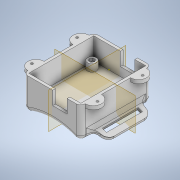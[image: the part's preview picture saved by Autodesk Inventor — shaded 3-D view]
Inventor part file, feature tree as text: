
AUTODESK INVENTOR PART (.ipt)
format: ipt  version: 2021 (Build 250183000, 183)  size: 576,000 bytes
history: native  units: mm
features: extrude x21, sketch x19, fillet x11, mirror x6, plane x2, pattern_linear x1, projected_geometry x1
ambient origin geometry x8: Origin, YZ Plane, XZ Plane, XY Plane, X Axis, Y Axis, Z Axis, Center Point
bodies: Solid1 (feature_tree)
feature tree (61):
  sketch  "Sketch1"  dims[d0=76.0mm d1=90.0mm]
  extrude  "Extrusion2"  Depth=90.0mm
  extrude  "Extrusion3"  Depth=3.0mm TaperAngle=0.0deg
  extrude  "Extrusion4"  Depth=10.0mm
  extrude  "Extrusion5"  Depth=3.0mm TaperAngle=0.0deg
  pattern_linear  "Rectangular Pattern1"  Count1=2 Spacing1=56.07mm
  sketch  "Sketch5"  dims[d12=6.0mm]
  extrude  "Extrusion6"  Depth=9.0mm TaperAngle=0.0deg
  extrude  "Extrusion7"  Depth=3.0mm TaperAngle=0.0deg
  sketch  "Sketch6"  dims[d13=2.7mm d14=0.0mm]
  extrude  "Extrusion8"  Depth=3.0mm TaperAngle=0.0deg
  extrude  "Extrusion9"  Depth=3.0mm TaperAngle=0.0deg
  plane  "Work Plane1"
  mirror  "Mirror1"
  sketch  "Sketch14"  dims[d15=3.3mm]
  extrude  "Extrusion15"  Depth=6.68mm
  extrude  "Extrusion17"  Depth=10.0mm TaperAngle=0.0deg
  extrude  "Extrusion18"  Depth=4.0mm TaperAngle=0.0deg
  mirror  "Mirror5"
  plane  "Work Plane3"
  mirror  "Mirror6"
  extrude  "Extrusion22"  Depth=4.0mm
  fillet  "Fillet9"  Radius=4.0mm
  extrude  "Extrusion26"  Depth=3.0mm
  extrude  "Extrusion27"  Depth=15.0mm TaperAngle=0.0deg
  fillet  "Fillet12"  Radius=40.0mm
  fillet  "Fillet13"  Radius=5.0mm
  mirror  "Mirror9"
  fillet  "Fillet14"  Radius=5.0mm
  fillet  "Fillet15"  Radius=20.0mm
  extrude  "Extrusion23"  Depth=3.0mm
  extrude  "Extrusion24"  Depth=3.0mm
  fillet  "Fillet10"  Radius=3.0mm
  mirror  "Mirror8"
  fillet  "Fillet11"  Radius=70.0mm
  extrude  "Extrusion25"  Depth=10.0mm TaperAngle=0.0deg
  extrude  "Extrusion19"  Depth=4.0mm
  extrude  "Extrusion20"  Depth=4.0mm
  extrude  "Extrusion21"  Depth=4.0mm
  fillet  "Fillet5"  Radius=15.0mm
  fillet  "Fillet6"  Radius=40.0mm
  mirror  "Mirror7"
  fillet  "Fillet7"  Radius=5.0mm
  fillet  "Fillet8"  Radius=5.0mm
  extrude  "Extrusion1"  Depth=4.0mm TaperAngle=0.0deg
  sketch  "Sketch2"  dims[d2=3.0mm d3=30.0mm d4=0.0mm]
  sketch  "Sketch3"  dims[d5=3.0mm d6=0.0mm d7=10.0mm]
  sketch  "Sketch4"  dims[d8=3.0mm d10=8.0mm d11=0.0mm]
  sketch  "Sketch15"  dims[d16=9.0mm d17=0.0mm d18=20.0mm d20=56.07mm d21=20.0mm d23=45.71mm]
  projected_geometry  "Projected Loop3"
  sketch  "Sketch19"  dims[d24=5.0mm d25=9.0mm d26=0.0mm]
  sketch  "Sketch20"  dims[d27=3.0mm d28=24.5mm d29=0.0mm]
  sketch  "Sketch21"  dims[d30=16.0mm d31=3.0mm d32=0.0mm]
  sketch  "Sketch22"  dims[d36=16.0mm d37=3.0mm d38=0.0mm]
  sketch  "Sketch23"  dims[d39=18.0mm d62=6.68mm]
  sketch  "Sketch24"  dims[d63=1.7mm d64=10.0mm d65=0.0mm]
  sketch  "Sketch25"  dims[d71=9.0mm d72=4.0mm d73=0.0mm]
  sketch  "Sketch26"  dims[d74=2.5mm d75=4.5mm d76=4.0mm d77=0.0mm]
  sketch  "Sketch27"  dims[d78=4.0mm d79=0.0mm d80=3.0mm]
  sketch  "Sketch29"  dims[d81=50.0mm d82=15.0mm d83=0.0mm d84=40.0mm d85=5.0mm d86=5.0mm d87=20.0mm d88=0.0mm]
  sketch  "Sketch30"  dims[d89=3.0mm d90=3.0mm d91=3.0mm d92=3.0mm d93=70.0mm d94=10.0mm d95=0.0mm d96=5.0mm d97=50.0mm d98=4.0mm d99=15.0mm d100=0.0mm d101=40.0mm d102=5.0mm d103=5.0mm d104=15.0mm d105=0.0mm d106=8.0mm d107=8.0mm d108=15.0mm d109=0.0mm d113=50.0mm d114=0.0mm d115=3.0mm d116=15.0mm d117=12.391838mm d118=40.0mm d119=5.0mm d120=5.0mm d121=50.0mm d122=0.0mm d123=8.0mm d124=4.0mm d125=8.0mm d126=4.0mm]
